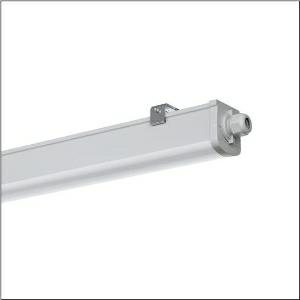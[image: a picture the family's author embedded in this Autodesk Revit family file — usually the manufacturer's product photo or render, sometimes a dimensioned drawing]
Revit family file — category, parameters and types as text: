
# Revit family: monsun_r__31_51fa207k450b_1d2e
name_source: partatom
category: Lighting Fixtures
units: mm (PartAtom-declared; Revit-internal decimal feet)

## family parameters
Cut with Voids When Loaded = No
Host = Face
Light Source = No
Part Type = Normal
Room Calculation Point = No
Round Connector Dimension = Use Diameter
Shared = No

## types (1)
- Monsun® 31 (1 x LED, 5100 lm, 38 W, 4000K)
    Apparent Load = 38 VA
    CIE Flux Codes = 42 72 91 92 100
    Color Rendering = 80
    Color Temperature = 4000K
    Default Elevation = 1800 mm
    Description = Monsun® 31, damp-proof luminaire, primary optical cover: diffuser, of PC, frosted, light emission: direct distribution, primary light characteristic: symmetric, installation type: surface-mounted, LED, rated luminous flux: 5.100lm, luminous efficacy: 134lm/W, light colour: 840, colour temperature: 4000K, control gear: ON/OFF, with terminal, 3+1-pole, max. 2.5mm², through-wiring: 3x 2.5mm² + 1x 1.5mm², mains connection: 220..240V, AC, 50/60Hz, rated input power: 38W, housing, luminaire housing, of PC, light grey (RAL 7035), length: 1.158mm, width: 68mm, height: 76mm, protection rating (complete): IP66, insulation class (complete): insulation class II (safety insulation), certification: CE, ENEC, UKCA, protection symbol: D, impact resistance: IK08, permissible operating ambient temperature: -20..+40°C, corresponds to IFS (International Featured Standards) requirements for safety and quality in the food industry, contact your sales advisor before using the luminaires in applications with unclear chemical exposure, large temperature fluctuations or condensation-forming humidity, packaging unit: 1 piece
    Height = 77 mm
    Lamp = 1 x LED
    Lamp Light Flux = 5100 lm
    Lamp Power = 38 W
    Lamp count = 1
    Length = 1218 mm
    Luminous efficacy = 134 lm/W
    Manufacturer = Siteco
    ModVariant = No
    Model = 51FA207K450B
    Mounting Place = Ceiling
    Mounting Type = Surface mounted
    Number of Poles = 1
    OnlyDefault = Yes
    Power Factor = 1
    Product Name = Monsun® 31
    Product group = damp-proof luminaire
    ProductGroupID = 301
    Protection Class = Protection class II
    Protection Degree = IP 66
    RLX_Detail_Level = 1
    RLX_Emergency_Light_Flux = 0 lm
    RLX_Emergency_Type = 0
    RLX_Emergency_Type_DB = No
    RlxData = <blob elided: 33001 chars, md5=4f671c55>
    Socket = socket
    Standby Power = 0 W
    System Light Flux = 5100 lm
    System Power = 38 W
    Type Comments = Product without accessories
    Type Image = l_1006174.jpg
    URL = http://relux.com
    VarID = ---
    Voltage = 0 V
    Weight = 0.00 kg
    Width = 69 mm

## geometry (parser evidence)
native form markers: Blend x4, Sweep x12
no freeform markers — native parametric forms only
